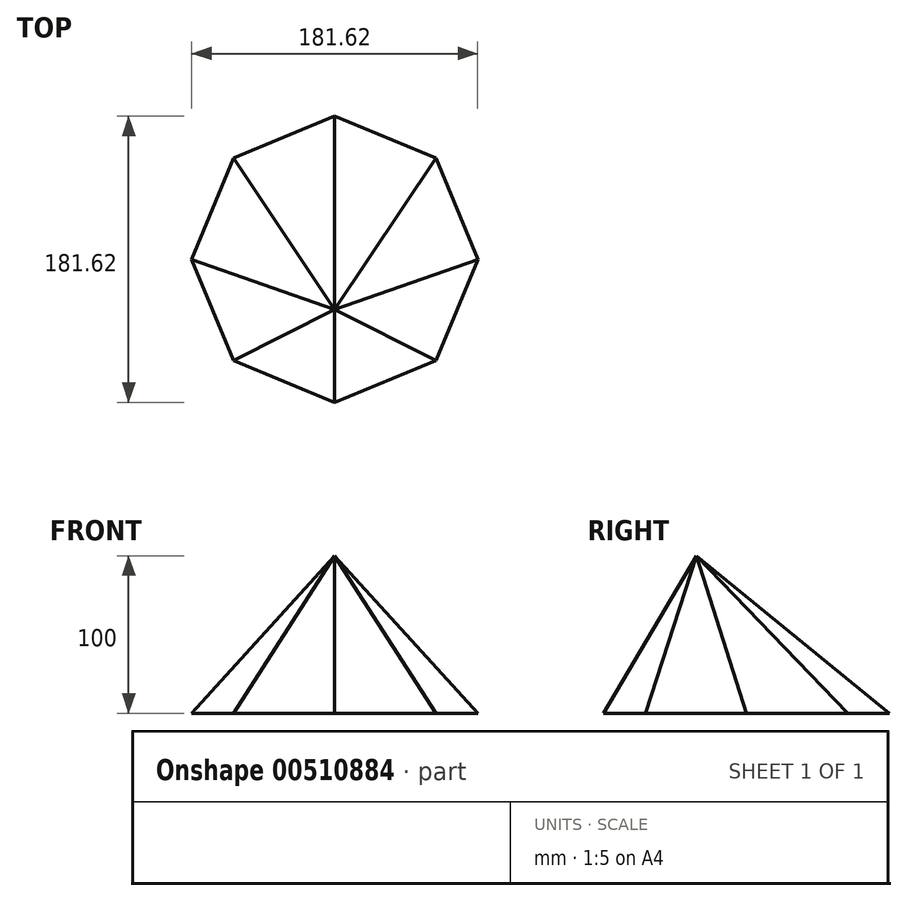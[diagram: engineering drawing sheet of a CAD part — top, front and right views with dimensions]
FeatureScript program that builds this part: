
annotation { "Feature Type Name" : "Feature", "Feature Type Description" : "" }
export const myFeature = defineFeature(function(context is Context, id is Id, definition is map)
    precondition{}
    {
        {
            var Q0;
            Q0=qCreatedBy(makeId("Top.planeOp"),FACE);
            var sketch = newSketch(context, id + "F0", { "sketchPlane" : qUnion([Q0])});
            skCircle(sketch, "E0.cCircle", {"center": v(0, 0) * mm, "radius": 90.81 * mm, "construction": true});
            skLineSegment(sketch, "E0.0", {"start": v(0, -90.81) * mm, "end": v(-64.21, -64.21) * mm});
            skLineSegment(sketch, "E0.1", {"start": v(-64.21, -64.21) * mm, "end": v(-90.81, 0) * mm});
            skLineSegment(sketch, "E0.2", {"start": v(-90.81, 0) * mm, "end": v(-64.21, 64.21) * mm});
            skLineSegment(sketch, "E0.3", {"start": v(-64.21, 64.21) * mm, "end": v(0, 90.81) * mm});
            skLineSegment(sketch, "E0.4", {"start": v(0, 90.81) * mm, "end": v(64.21, 64.21) * mm});
            skLineSegment(sketch, "E0.5", {"start": v(64.21, 64.21) * mm, "end": v(90.81, 0) * mm});
            skLineSegment(sketch, "E0.6", {"start": v(90.81, 0) * mm, "end": v(64.21, -64.21) * mm});
            skLineSegment(sketch, "E0.7", {"start": v(64.21, -64.21) * mm, "end": v(0, -90.81) * mm});
            skSolve(sketch);
        }
        {
            var Q0;
            Q0=qCreatedBy(makeId("Top.planeOp"),FACE);
            cPlane(context, id + "F1", {"entities" : qUnion([Q0]), "cplaneType" : CPlaneType.OFFSET, "offset" : 100 * mm, "width" : 150 * mm, "height" : 150 * mm});
        }
        {
            var Q0;
            Q0=qCreatedBy(id+"F1.planeOp",FACE);
            var sketch = newSketch(context, id + "F2", { "sketchPlane" : qUnion([Q0])});
            skPoint(sketch, "E1", {"position": v(0, -6.45) * mm});
            skPoint(sketch, "E2", {"position": v(0, -31.84) * mm});
            skSolve(sketch);
        }
        {
            var Q0;
            Q0=sQuery(id+"F2.wireOp",VERTEX,"E2");
            var Q1;
            Q1=makeQuery(id+"F0.imprint","IMPRINT",FACE,{"disambiguationData":[TD([[makeQuery(id+"F0.imprint","IMPRINT",EDGE,{"derivedFrom":sQuery(id+"F0.wireOp",EDGE,"E0.0")}),-1.0]])]});
            loft(context, id + "F3", {"sheetProfilesArray" : [{ "sheetProfileEntities" : qUnion([Q0]) }, { "sheetProfileEntities" : qUnion([Q1]) }]});
        }
    });
